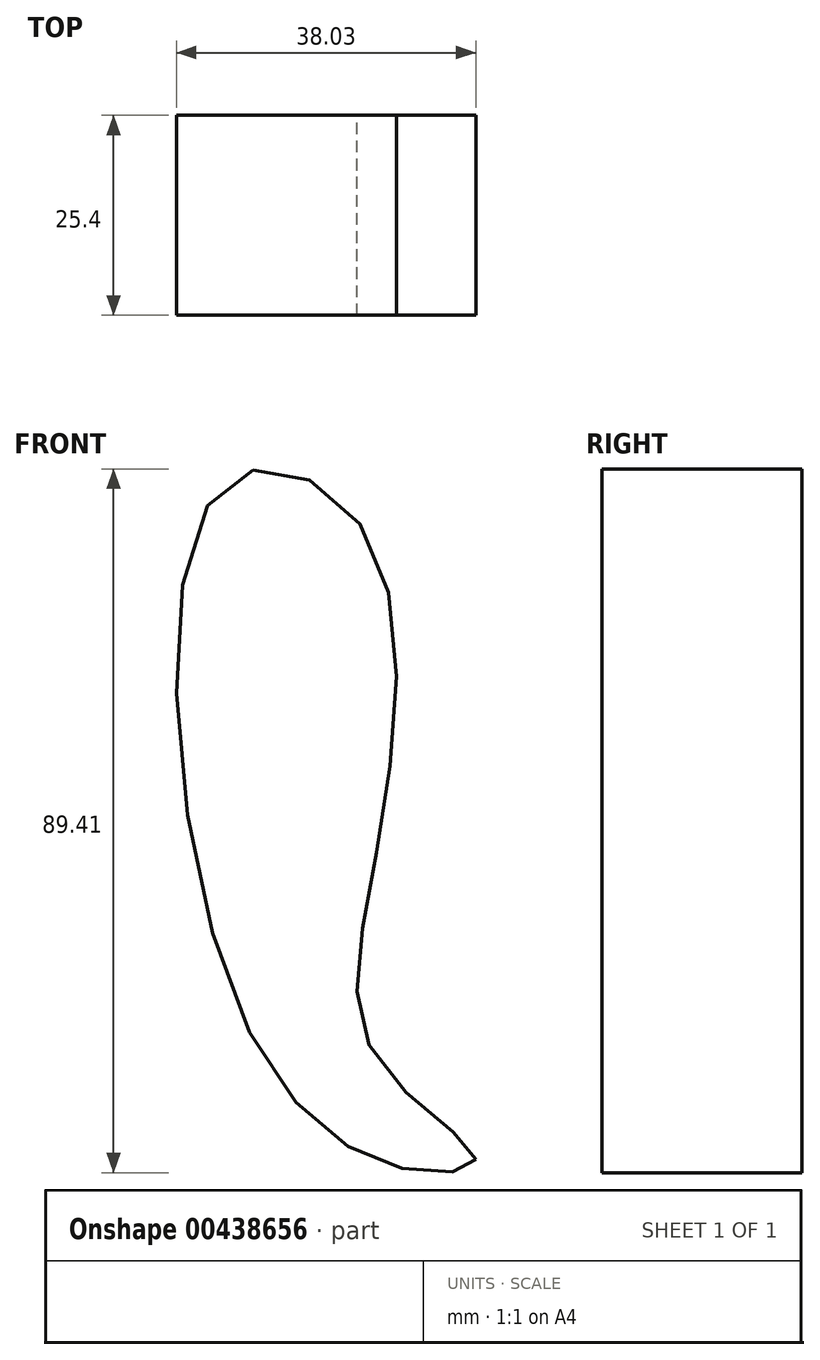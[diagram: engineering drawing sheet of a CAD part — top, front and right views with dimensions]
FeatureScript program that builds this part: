
annotation { "Feature Type Name" : "Feature", "Feature Type Description" : "" }
export const myFeature = defineFeature(function(context is Context, id is Id, definition is map)
    precondition{}
    {
        {
            var Q0;
            Q0=qCreatedBy(makeId("Front.planeOp"),FACE);
            var sketch = newSketch(context, id + "F0", { "sketchPlane" : qUnion([Q0])});
            skCircle(sketch, "E0", {"center": v(0, 0) * mm, "radius": 25.46 * mm});
            skFitSpline(sketch, "E1", {"points": [v(-19.07, -18.84) * mm, v(-26.98, -20.24) * mm, v(-49.08, 0) * mm, v(-51.17, 66.75) * mm, v(-33.03, 60.7) * mm, v(-32.33, 16.75) * mm, v(-31.17, -6.75) * mm, v(-19.07, -18.84) * mm]});
            skSolve(sketch);
        }
        {
            var Q0;
            Q0=makeQuery(id+"F0.imprint","IMPRINT",FACE,{"disambiguationData":[TD([[makeQuery(id+"F0.imprint","IMPRINT",EDGE,{"derivedFrom":sQuery(id+"F0.wireOp",EDGE,"E1")}),-1.0]])]});
            extrude(context, id + "F1", {"entities" : qUnion([Q0]), "depth" : 25.4 * mm});
        }
    });
